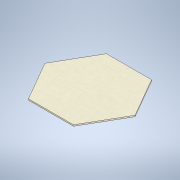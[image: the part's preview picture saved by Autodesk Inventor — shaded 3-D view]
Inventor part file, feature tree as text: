
AUTODESK INVENTOR PART (.ipt)
format: ipt  version: 2021 (Build 250183000, 183)  size: 105,984 bytes
history: native  units: mm
features: extrude x1, sketch x1
ambient origin geometry x8: Origin, YZ Plane, XZ Plane, XY Plane, X Axis, Y Axis, Z Axis, Center Point
bodies: Solid1 (feature_tree)
feature tree (2):
  extrude  "Extrusion1"  Depth=1.7mm TaperAngle=0.0deg
  sketch  "Sketch1"  dims[d0=101.0mm d1=1.7mm d2=0.0mm]
